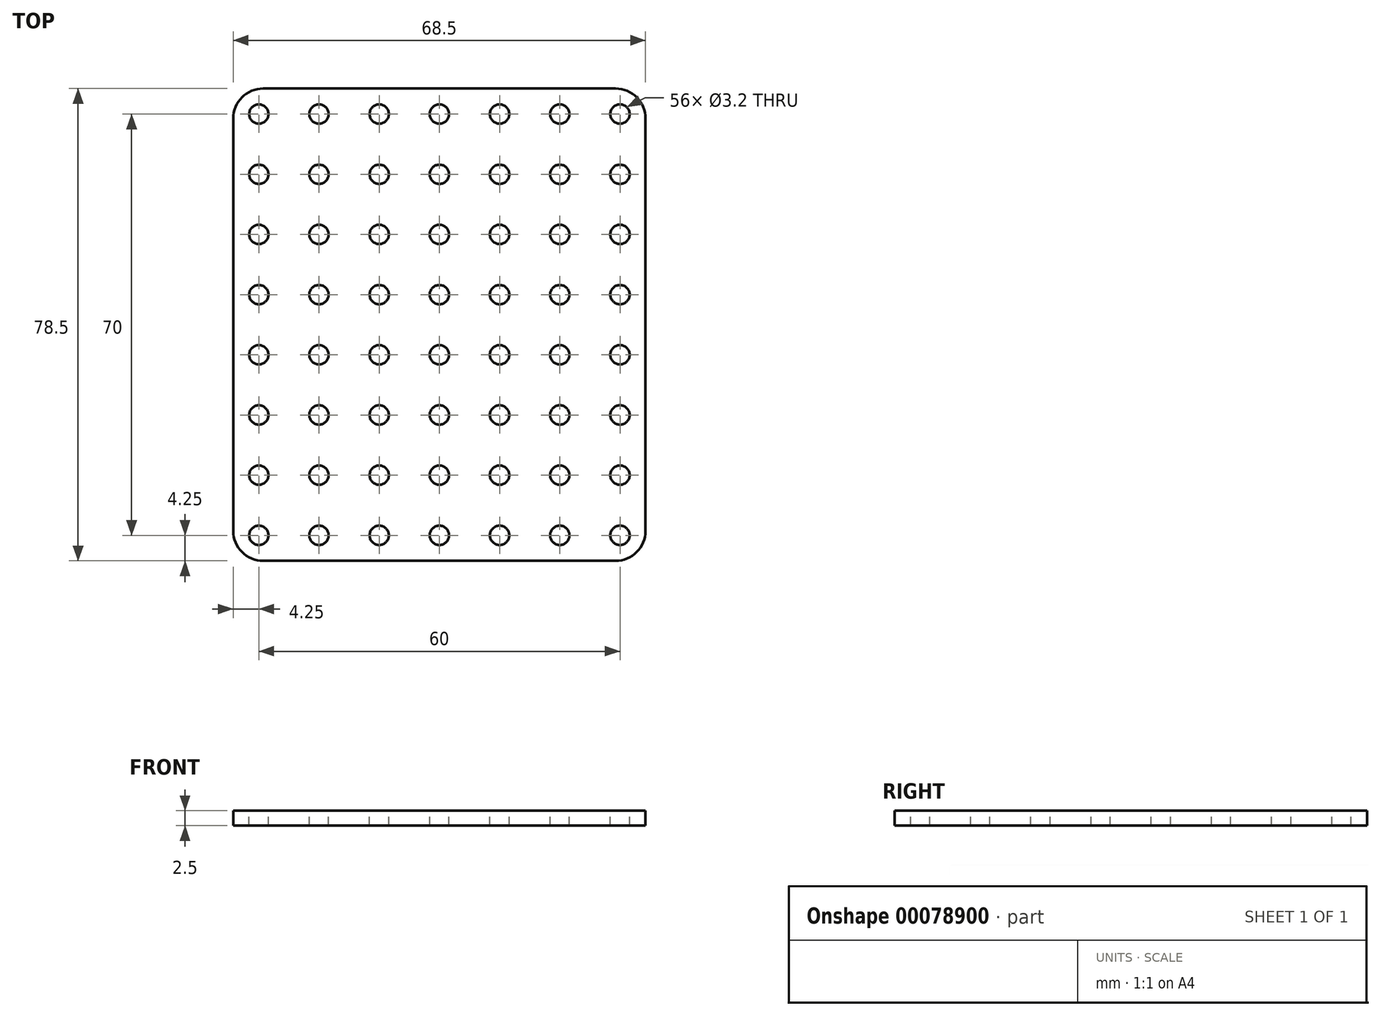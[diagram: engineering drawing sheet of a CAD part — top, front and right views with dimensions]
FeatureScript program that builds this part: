
annotation { "Feature Type Name" : "Feature", "Feature Type Description" : "" }
export const myFeature = defineFeature(function(context is Context, id is Id, definition is map)
    precondition{}
    {
        {
            var Q0;
            Q0=qCreatedBy(makeId("Top.planeOp"),FACE);
            var sketch = newSketch(context, id + "F0", { "sketchPlane" : qUnion([Q0])});
            skLineSegment(sketch, "E0.bottom", {"start": v(34.25, 39.25) * mm, "end": v(-34.25, 39.25) * mm});
            skLineSegment(sketch, "E0.top", {"start": v(34.25, -39.25) * mm, "end": v(-34.25, -39.25) * mm});
            skLineSegment(sketch, "E0.left", {"start": v(34.25, 39.25) * mm, "end": v(34.25, -39.25) * mm});
            skLineSegment(sketch, "E0.right", {"start": v(-34.25, 39.25) * mm, "end": v(-34.25, -39.25) * mm});
            skPoint(sketch, "E0.middle", {"position": v(0, 0) * mm});
            skCircle(sketch, "E1", {"center": v(-30, 35) * mm, "radius": 1.6 * mm});
            skCircle(sketch, "E2.0.1.0", {"center": v(-30, 25) * mm, "radius": 1.6 * mm});
            skCircle(sketch, "E2.0.2.0", {"center": v(-30, 15) * mm, "radius": 1.6 * mm});
            skCircle(sketch, "E2.0.3.0", {"center": v(-30, 5) * mm, "radius": 1.6 * mm});
            skCircle(sketch, "E2.0.4.0", {"center": v(-30, -5) * mm, "radius": 1.6 * mm});
            skCircle(sketch, "E2.0.5.0", {"center": v(-30, -15) * mm, "radius": 1.6 * mm});
            skCircle(sketch, "E2.0.6.0", {"center": v(-30, -25) * mm, "radius": 1.6 * mm});
            skCircle(sketch, "E2.0.7.0", {"center": v(-30, -35) * mm, "radius": 1.6 * mm});
            skCircle(sketch, "E2.1.0.0", {"center": v(-20, 35) * mm, "radius": 1.6 * mm});
            skCircle(sketch, "E2.1.1.0", {"center": v(-20, 25) * mm, "radius": 1.6 * mm});
            skCircle(sketch, "E2.1.2.0", {"center": v(-20, 15) * mm, "radius": 1.6 * mm});
            skCircle(sketch, "E2.1.3.0", {"center": v(-20, 5) * mm, "radius": 1.6 * mm});
            skCircle(sketch, "E2.1.4.0", {"center": v(-20, -5) * mm, "radius": 1.6 * mm});
            skCircle(sketch, "E2.1.5.0", {"center": v(-20, -15) * mm, "radius": 1.6 * mm});
            skCircle(sketch, "E2.1.6.0", {"center": v(-20, -25) * mm, "radius": 1.6 * mm});
            skCircle(sketch, "E2.1.7.0", {"center": v(-20, -35) * mm, "radius": 1.6 * mm});
            skCircle(sketch, "E2.2.0.0", {"center": v(-10, 35) * mm, "radius": 1.6 * mm});
            skCircle(sketch, "E2.2.1.0", {"center": v(-10, 25) * mm, "radius": 1.6 * mm});
            skCircle(sketch, "E2.2.2.0", {"center": v(-10, 15) * mm, "radius": 1.6 * mm});
            skCircle(sketch, "E2.2.3.0", {"center": v(-10, 5) * mm, "radius": 1.6 * mm});
            skCircle(sketch, "E2.2.4.0", {"center": v(-10, -5) * mm, "radius": 1.6 * mm});
            skCircle(sketch, "E2.2.5.0", {"center": v(-10, -15) * mm, "radius": 1.6 * mm});
            skCircle(sketch, "E2.2.6.0", {"center": v(-10, -25) * mm, "radius": 1.6 * mm});
            skCircle(sketch, "E2.2.7.0", {"center": v(-10, -35) * mm, "radius": 1.6 * mm});
            skCircle(sketch, "E2.3.0.0", {"center": v(0, 35) * mm, "radius": 1.6 * mm});
            skCircle(sketch, "E2.3.1.0", {"center": v(0, 25) * mm, "radius": 1.6 * mm});
            skCircle(sketch, "E2.3.2.0", {"center": v(0, 15) * mm, "radius": 1.6 * mm});
            skCircle(sketch, "E2.3.3.0", {"center": v(0, 5) * mm, "radius": 1.6 * mm});
            skCircle(sketch, "E2.3.4.0", {"center": v(0, -5) * mm, "radius": 1.6 * mm});
            skCircle(sketch, "E2.3.5.0", {"center": v(0, -15) * mm, "radius": 1.6 * mm});
            skCircle(sketch, "E2.3.6.0", {"center": v(0, -25) * mm, "radius": 1.6 * mm});
            skCircle(sketch, "E2.3.7.0", {"center": v(0, -35) * mm, "radius": 1.6 * mm});
            skCircle(sketch, "E2.4.0.0", {"center": v(10, 35) * mm, "radius": 1.6 * mm});
            skCircle(sketch, "E2.4.1.0", {"center": v(10, 25) * mm, "radius": 1.6 * mm});
            skCircle(sketch, "E2.4.2.0", {"center": v(10, 15) * mm, "radius": 1.6 * mm});
            skCircle(sketch, "E2.4.3.0", {"center": v(10, 5) * mm, "radius": 1.6 * mm});
            skCircle(sketch, "E2.4.4.0", {"center": v(10, -5) * mm, "radius": 1.6 * mm});
            skCircle(sketch, "E2.4.5.0", {"center": v(10, -15) * mm, "radius": 1.6 * mm});
            skCircle(sketch, "E2.4.6.0", {"center": v(10, -25) * mm, "radius": 1.6 * mm});
            skCircle(sketch, "E2.4.7.0", {"center": v(10, -35) * mm, "radius": 1.6 * mm});
            skCircle(sketch, "E2.5.0.0", {"center": v(20, 35) * mm, "radius": 1.6 * mm});
            skCircle(sketch, "E2.5.1.0", {"center": v(20, 25) * mm, "radius": 1.6 * mm});
            skCircle(sketch, "E2.5.2.0", {"center": v(20, 15) * mm, "radius": 1.6 * mm});
            skCircle(sketch, "E2.5.3.0", {"center": v(20, 5) * mm, "radius": 1.6 * mm});
            skCircle(sketch, "E2.5.4.0", {"center": v(20, -5) * mm, "radius": 1.6 * mm});
            skCircle(sketch, "E2.5.5.0", {"center": v(20, -15) * mm, "radius": 1.6 * mm});
            skCircle(sketch, "E2.5.6.0", {"center": v(20, -25) * mm, "radius": 1.6 * mm});
            skCircle(sketch, "E2.5.7.0", {"center": v(20, -35) * mm, "radius": 1.6 * mm});
            skCircle(sketch, "E2.6.0.0", {"center": v(30, 35) * mm, "radius": 1.6 * mm});
            skCircle(sketch, "E2.6.1.0", {"center": v(30, 25) * mm, "radius": 1.6 * mm});
            skCircle(sketch, "E2.6.2.0", {"center": v(30, 15) * mm, "radius": 1.6 * mm});
            skCircle(sketch, "E2.6.3.0", {"center": v(30, 5) * mm, "radius": 1.6 * mm});
            skCircle(sketch, "E2.6.4.0", {"center": v(30, -5) * mm, "radius": 1.6 * mm});
            skCircle(sketch, "E2.6.5.0", {"center": v(30, -15) * mm, "radius": 1.6 * mm});
            skCircle(sketch, "E2.6.6.0", {"center": v(30, -25) * mm, "radius": 1.6 * mm});
            skCircle(sketch, "E2.6.7.0", {"center": v(30, -35) * mm, "radius": 1.6 * mm});
            skLineSegment(sketch, "E2.direction1", {"start": v(-30, 35) * mm, "end": v(-20, 35) * mm, "construction": true});
            skLineSegment(sketch, "E2.direction2", {"start": v(-30, 35) * mm, "end": v(-30, 25) * mm, "construction": true});
            skSolve(sketch);
        }
        {
            var Q0;
            Q0=makeQuery(id+"F0.imprint","IMPRINT",FACE,{"disambiguationData":[TD([[makeQuery(id+"F0.imprint","IMPRINT",EDGE,{"derivedFrom":sQuery(id+"F0.wireOp",EDGE,"E0.bottom")}),1.0]])]});
            extrude(context, id + "F1", {"entities" : qUnion([Q0]), "oppositeDirection" : true, "depth" : 2.5 * mm});
        }
        {
            var Q0;
            Q0=makeQuery(id+"F1.opExtrude","SWEPT_EDGE",EDGE,{"disambiguationData":[OSD([sQuery(id+"F0.wireOp",EDGE,"E0.bottom"),sQuery(id+"F0.wireOp",EDGE,"E0.left")])]});
            var Q1;
            Q1=makeQuery(id+"F1.opExtrude","SWEPT_EDGE",EDGE,{"disambiguationData":[OSD([sQuery(id+"F0.wireOp",EDGE,"E0.top"),sQuery(id+"F0.wireOp",EDGE,"E0.right")])]});
            var Q2;
            Q2=makeQuery(id+"F1.opExtrude","SWEPT_EDGE",EDGE,{"disambiguationData":[OSD([sQuery(id+"F0.wireOp",EDGE,"E0.top"),sQuery(id+"F0.wireOp",EDGE,"E0.left")])]});
            var Q3;
            Q3=makeQuery(id+"F1.opExtrude","SWEPT_EDGE",EDGE,{"disambiguationData":[OSD([sQuery(id+"F0.wireOp",EDGE,"E0.bottom"),sQuery(id+"F0.wireOp",EDGE,"E0.right")])]});
            fillet(context, id + "F2", {"entities" : qUnion([Q0, Q1, Q2, Q3]), "radius" : 5 * mm, "tangentPropagation" : true, "allowEdgeOverflow" : false});
        }
    });
